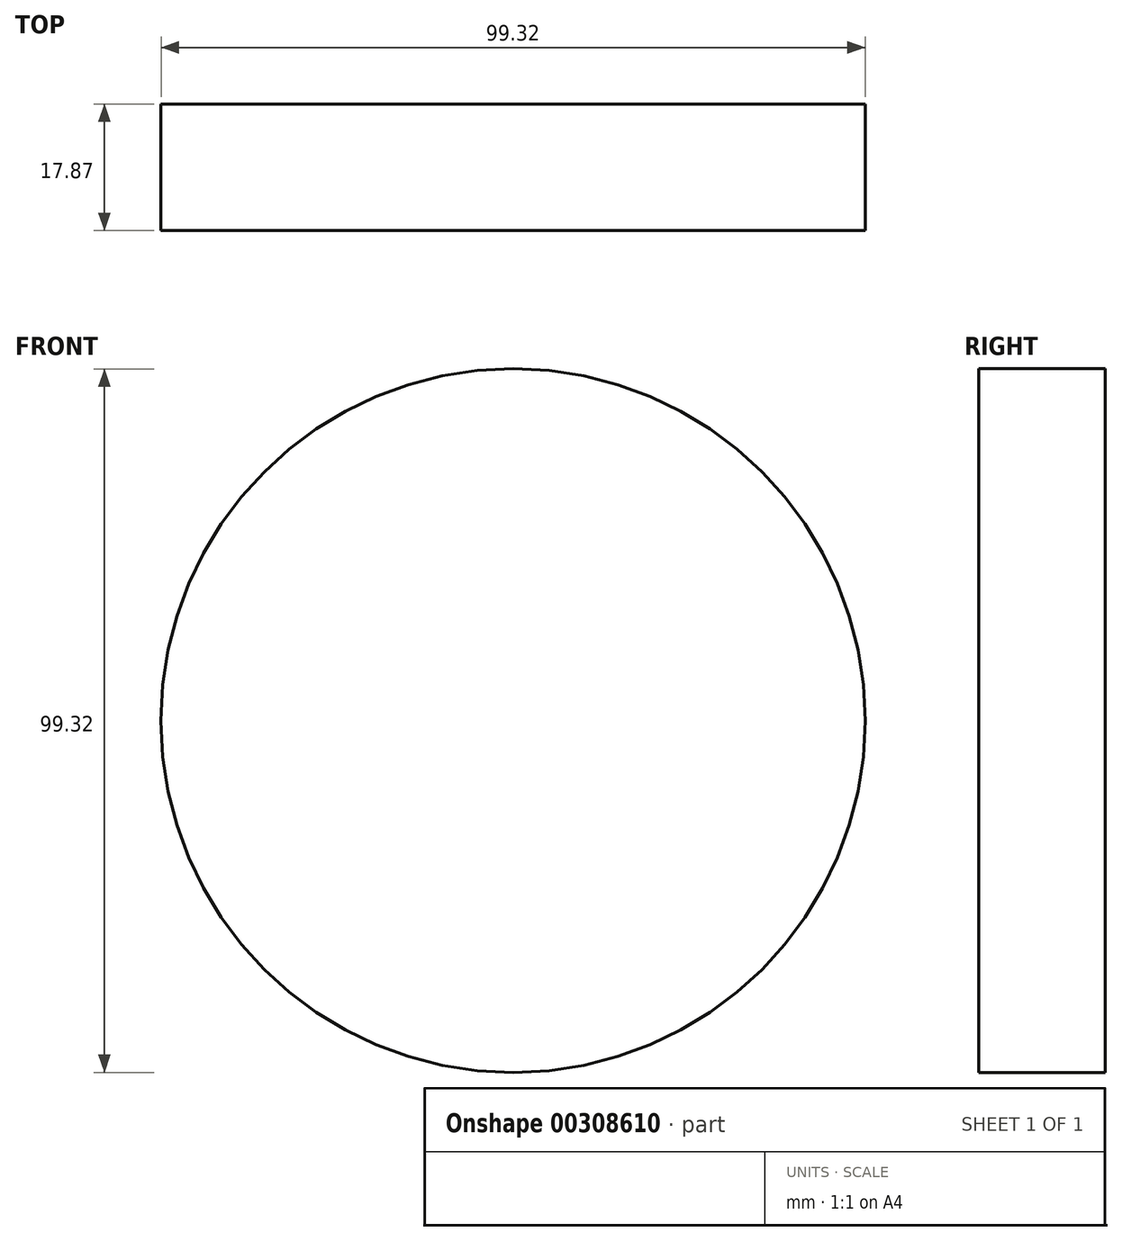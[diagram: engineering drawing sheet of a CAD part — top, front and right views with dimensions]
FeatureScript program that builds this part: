
annotation { "Feature Type Name" : "Feature", "Feature Type Description" : "" }
export const myFeature = defineFeature(function(context is Context, id is Id, definition is map)
    precondition{}
    {
        {
            var Q0;
            Q0=qCreatedBy(makeId("Front.planeOp"),FACE);
            var sketch = newSketch(context, id + "F0", { "sketchPlane" : qUnion([Q0])});
            skCircle(sketch, "E0", {"center": v(0, 0) * mm, "radius": 49.66 * mm});
            skSolve(sketch);
        }
        {
            var Q0;
            Q0=makeQuery(id+"F0.imprint","IMPRINT",FACE,{"disambiguationData":[TD([[makeQuery(id+"F0.imprint","IMPRINT",EDGE,{"derivedFrom":sQuery(id+"F0.wireOp",EDGE,"E0")}),1.0]])]});
            extrude(context, id + "F1", {"entities" : qUnion([Q0]), "depth" : 17.87 * mm});
        }
    });
